# Revit family: Cabinet_Accessories-Danver-Side_Panel
name_source: partatom
category: Casework
units: mm (PartAtom-declared; Revit-internal decimal feet)

## family parameters
Always vertical = Yes
Cut with Voids When Loaded = No
Room Calculation Point = No
Shared = No
Work Plane-Based = No

## types (4) — shared parameters
Construction Type = Type 304 Stainless Steel
Default Elevation = 0"
Door Style = Door : Hampton
Handle Material = Metal - Danver - Chrome Plated Steel
Keynote = 12 35 28
Manufacturer = Danver Outdoor Kitchens
Panel Height = 2' - 6"
Panel Material = Metal - Danver - Stainless Steel
Panel Thickness = 3/4"
Product Documentation Link = https://danver.com
Product Page URL = https://danver.com
Threshold Offset = 1 1/4"
Toe Kick Material = Metal - Danver - Toe Kick
URL = www.danver.com
Version = 2019 - V1.0B

## per-type parameters (varying)
| type | Base Cab Depth | Description | Model | Panel Width | Toe Kick Length |
| 27.88 Width | 2' - 3" | Left Side Panel - 27 7/8" Wide x 30" Tall x 3/4" Thick | OSP KW LV 27.88L | 2' - 3 7/8" | 2' - 1 3/4" |
| 24.88 Width | 2' - 0" | Left Side Panel - 24 7/8" Wide x 30" Tall x 3/4" Thick | OSP KW LV 24.88L | 2' - 0 7/8" | 1' - 10 3/4" |
| 25.63 Width | 2' - 0 3/4" | Left Side Panel - 25 5/8" Wide x 30" Tall x 3/4" Thick | OSP KW LV 25.63L | 2' - 1 5/8" | 1' - 11 1/2" |
| 28.63 Width | 2' - 3 3/4" | Left Side Panel - 28 5/8" Wide x 30" Tall x 3/4" Thick | OSP KW LV 28.63L | 2' - 4 5/8" | 2' - 2 1/2" |

## geometry (parser evidence)
native form markers: Sweep x10
no freeform markers — native parametric forms only
